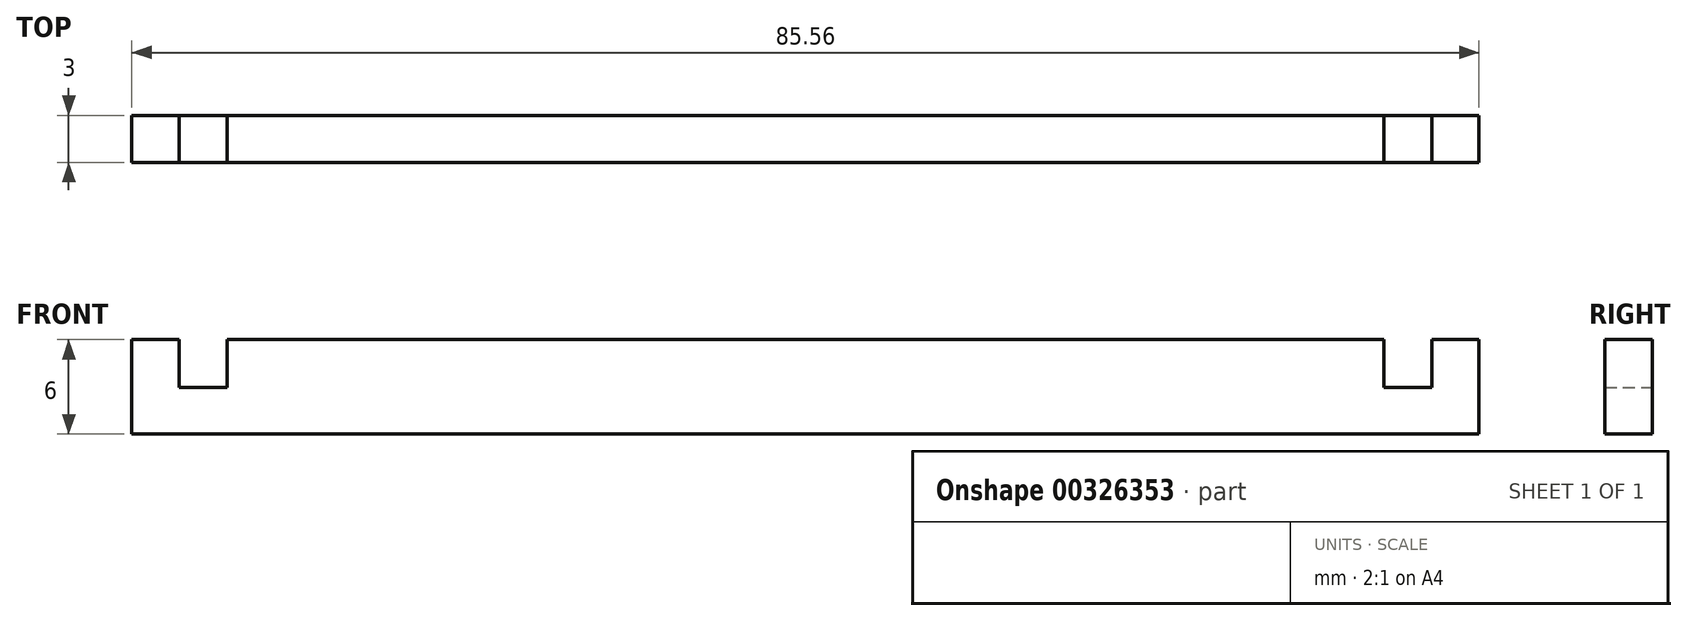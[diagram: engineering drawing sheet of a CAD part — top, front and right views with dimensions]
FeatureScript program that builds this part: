
annotation { "Feature Type Name" : "Feature", "Feature Type Description" : "" }
export const myFeature = defineFeature(function(context is Context, id is Id, definition is map)
    precondition{}
    {
        {
            var Q0;
            Q0=qCreatedBy(makeId("Front.planeOp"),FACE);
            var sketch = newSketch(context, id + "F0", { "sketchPlane" : qUnion([Q0])});
            skLineSegment(sketch, "E0", {"start": v(-42.78, -3.23) * mm, "end": v(-42.78, 2.77) * mm});
            skLineSegment(sketch, "E1", {"start": v(-42.78, 2.77) * mm, "end": v(-39.78, 2.77) * mm});
            skLineSegment(sketch, "E2", {"start": v(42.78, 2.77) * mm, "end": v(42.78, -3.23) * mm});
            skPoint(sketch, "E3", {"position": v(-39.78, -0.25) * mm});
            skPoint(sketch, "E4", {"position": v(-36.74, -0.25) * mm});
            skPoint(sketch, "E5", {"position": v(39.78, -0.25) * mm});
            skPoint(sketch, "E6", {"position": v(36.74, -0.25) * mm});
            skLineSegment(sketch, "E7", {"start": v(-36.74, -0.25) * mm, "end": v(-39.78, -0.25) * mm});
            skLineSegment(sketch, "E8", {"start": v(39.78, -0.25) * mm, "end": v(36.74, -0.25) * mm});
            skLineSegment(sketch, "E9", {"start": v(-42.78, -3.23) * mm, "end": v(42.78, -3.23) * mm});
            skLineSegment(sketch, "E10", {"start": v(39.78, -0.25) * mm, "end": v(39.78, 2.77) * mm});
            skLineSegment(sketch, "E11", {"start": v(36.74, -0.25) * mm, "end": v(36.74, 2.77) * mm});
            skLineSegment(sketch, "E12", {"start": v(-39.78, -0.25) * mm, "end": v(-39.78, 2.77) * mm});
            skLineSegment(sketch, "E13", {"start": v(-36.74, -0.25) * mm, "end": v(-36.74, 2.77) * mm});
            skLineSegment(sketch, "E14.trimOffspring", {"start": v(-36.74, 2.77) * mm, "end": v(36.74, 2.77) * mm});
            skLineSegment(sketch, "E15.trimOffspring", {"start": v(39.78, 2.77) * mm, "end": v(42.78, 2.77) * mm});
            skSolve(sketch);
        }
        {
            var Q0;
            Q0=makeQuery(id+"F0.imprint","IMPRINT",FACE,{"disambiguationData":[TD([[makeQuery(id+"F0.imprint","IMPRINT",EDGE,{"derivedFrom":sQuery(id+"F0.wireOp",EDGE,"E0")}),-1.0]])]});
            extrude(context, id + "F1", {"entities" : qUnion([Q0]), "depth" : 3 * mm});
        }
    });
